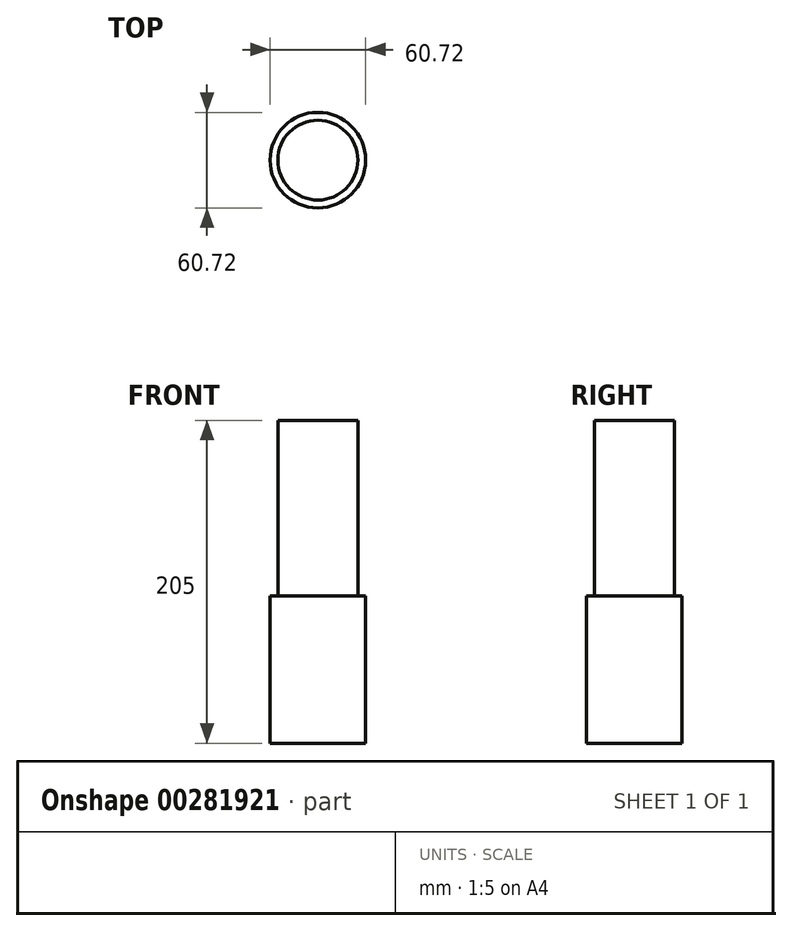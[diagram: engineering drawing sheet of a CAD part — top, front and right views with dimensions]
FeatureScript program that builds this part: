
annotation { "Feature Type Name" : "Feature", "Feature Type Description" : "" }
export const myFeature = defineFeature(function(context is Context, id is Id, definition is map)
    precondition{}
    {
        {
            var Q0;
            Q0=qCreatedBy(makeId("Front.planeOp"),FACE);
            var sketch = newSketch(context, id + "F0", { "sketchPlane" : qUnion([Q0])});
            skLineSegment(sketch, "E0.bottom", {"start": v(25.36, -46.5) * mm, "end": v(-25.36, -46.5) * mm});
            skLineSegment(sketch, "E0.top", {"start": v(25.36, 42.12) * mm, "end": v(-25.36, 42.12) * mm});
            skLineSegment(sketch, "E0.left", {"start": v(25.36, -46.5) * mm, "end": v(25.36, 42.12) * mm});
            skLineSegment(sketch, "E0.right", {"start": v(-25.36, -46.5) * mm, "end": v(-25.36, 42.12) * mm});
            skPoint(sketch, "E0.middle", {"position": v(0, -2.19) * mm});
            skLineSegment(sketch, "E1", {"start": v(0, 42.12) * mm, "end": v(0, -46.5) * mm});
            skSolve(sketch);
        }
        {
            var Q0;
            {var subQ0=sQuery(id+"F0.wireOp",EDGE,"E0.right");Q0=makeQuery(id+"F0.imprint","IMPRINT",FACE,{"disambiguationData":[TD([[makeQuery(id+"F0.imprint","IMPRINT",EDGE,{"derivedFrom":subQ0}),-1.0]])]});}
            var Q1;
            Q1=sQuery(id+"F0.wireOp",EDGE,"E1");
            revolve(context, id + "F1", {"entities" : qUnion([Q0]), "axis" : qUnion([Q1]), "revolveType" : RevolveType.FULL});
        }
        {
            var Q0;
            Q0=makeQuery(id+"F1.opRevolve","SWEPT_FACE",FACE,{"disambiguationData":[OSD([sQuery(id+"F0.wireOp",EDGE,"E0.top")])]});
            shell(context, id + "F2", {"entities" : qUnion([Q0]), "thickness" : 5 * mm, "oppositeDirection" : true});
        }
        {
            var Q0;
            Q0=makeQuery(id+"F2.opShell","OFFSET_FACE",FACE,{"disambiguationData":[OSD([sQuery(id+"F0.wireOp",EDGE,"E0.bottom")])]});
            extrude(context, id + "F3", {"entities" : qUnion([Q0]), "operationType" : NewBodyOperationType.ADD, "depth" : 200 * mm});
        }
    });
